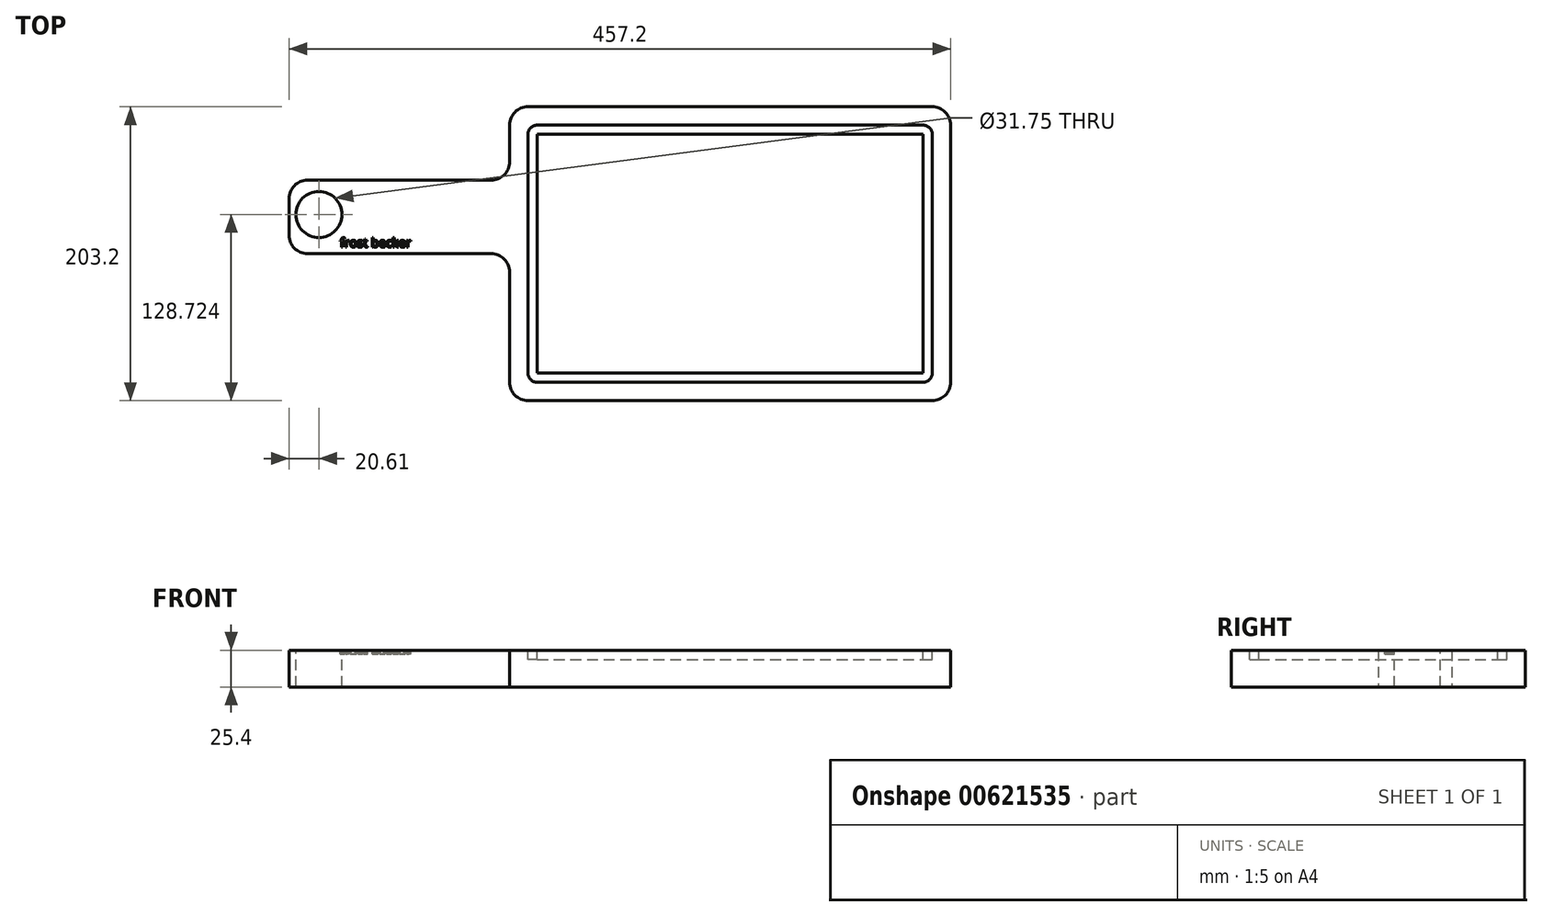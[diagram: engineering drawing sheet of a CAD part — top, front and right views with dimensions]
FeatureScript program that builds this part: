
annotation { "Feature Type Name" : "Feature", "Feature Type Description" : "" }
export const myFeature = defineFeature(function(context is Context, id is Id, definition is map)
    precondition{}
    {
        {
            var Q0;
            Q0=qCreatedBy(makeId("Top.planeOp"),FACE);
            var sketch = newSketch(context, id + "F0", { "sketchPlane" : qUnion([Q0])});
            skLineSegment(sketch, "E0.bottom", {"start": v(0, 0) * mm, "end": v(304.8, 0) * mm});
            skLineSegment(sketch, "E0.top", {"start": v(0, 203.2) * mm, "end": v(304.8, 203.2) * mm});
            skLineSegment(sketch, "E0.left", {"start": v(0, 0) * mm, "end": v(0, 203.2) * mm});
            skLineSegment(sketch, "E0.right", {"start": v(304.8, 0) * mm, "end": v(304.8, 203.2) * mm});
            skLineSegment(sketch, "E1.bottom", {"start": v(0, 101.6) * mm, "end": v(-152.4, 101.6) * mm});
            skLineSegment(sketch, "E1.top", {"start": v(0, 152.4) * mm, "end": v(-152.4, 152.4) * mm});
            skLineSegment(sketch, "E1.left", {"start": v(0, 101.6) * mm, "end": v(0, 152.4) * mm});
            skLineSegment(sketch, "E1.right", {"start": v(-152.4, 101.6) * mm, "end": v(-152.4, 152.4) * mm});
            skSolve(sketch);
        }
        {
            var Q0;
            Q0=makeQuery(id+"F0.imprint","IMPRINT",FACE,{"disambiguationData":[TD([[makeQuery(id+"F0.imprint","IMPRINT",EDGE,{"derivedFrom":sQuery(id+"F0.wireOp",EDGE,"E1.bottom")}),-1.0]])]});
            var Q1;
            {var subQ3=sQuery(id+"F0.wireOp",EDGE,"E0.bottom");Q1=makeQuery(id+"F0.imprint","IMPRINT",FACE,{"disambiguationData":[TD([[makeQuery(id+"F0.imprint","IMPRINT",EDGE,{"derivedFrom":subQ3}),1.0]])]});}
            extrude(context, id + "F1", {"entities" : qUnion([Q0, Q1]), "depth" : 25.4 * mm, "offsetDistance" : 25.4 * mm});
        }
        {
            var Q0;
            Q0=makeQuery(id+"F1.opExtrude","CAP_FACE",FACE,{"disambiguationData":[OSD([sQuery(id+"F0.wireOp",EDGE,"E0.bottom"),sQuery(id+"F0.wireOp",EDGE,"E0.top"),sQuery(id+"F0.wireOp",EDGE,"E0.left"),sQuery(id+"F0.wireOp",EDGE,"E0.right"),sQuery(id+"F0.wireOp",EDGE,"E1.bottom"),sQuery(id+"F0.wireOp",EDGE,"E1.top"),sQuery(id+"F0.wireOp",EDGE,"E1.right")])],"isStart":false});
            var sketch = newSketch(context, id + "F2", { "sketchPlane" : qUnion([Q0])});
            skCircle(sketch, "E2", {"center": v(-131.8, 128.72) * mm, "radius": 15.88 * mm});
            skLineSegment(sketch, "E3.0", {"start": v(12.7, 12.7) * mm, "end": v(12.7, 101.6) * mm});
            skLineSegment(sketch, "E3.1", {"start": v(12.7, 152.4) * mm, "end": v(12.7, 190.5) * mm});
            skLineSegment(sketch, "E3.2", {"start": v(12.7, 190.5) * mm, "end": v(292.1, 190.5) * mm});
            skLineSegment(sketch, "E3.3", {"start": v(292.1, 12.7) * mm, "end": v(292.1, 190.5) * mm});
            skLineSegment(sketch, "E3.4", {"start": v(12.7, 12.7) * mm, "end": v(292.1, 12.7) * mm});
            skLineSegment(sketch, "E4", {"start": v(12.7, 152.4) * mm, "end": v(12.7, 101.6) * mm});
            skLineSegment(sketch, "E5.0", {"start": v(19.05, 152.4) * mm, "end": v(19.05, 184.15) * mm});
            skLineSegment(sketch, "E5.1", {"start": v(285.75, 19.05) * mm, "end": v(285.75, 184.15) * mm});
            skLineSegment(sketch, "E5.2", {"start": v(19.05, 19.05) * mm, "end": v(285.75, 19.05) * mm});
            skLineSegment(sketch, "E5.3", {"start": v(19.05, 184.15) * mm, "end": v(285.75, 184.15) * mm});
            skLineSegment(sketch, "E5.4", {"start": v(19.05, 19.05) * mm, "end": v(19.05, 101.6) * mm});
            skLineSegment(sketch, "E5.5", {"start": v(19.05, 152.4) * mm, "end": v(19.05, 101.6) * mm});
            skSolve(sketch);
        }
        {
            var Q0;
            Q0=makeQuery(id+"F2.imprint","IMPRINT",FACE,{"disambiguationData":[TD([[makeQuery(id+"F2.imprint","IMPRINT",EDGE,{"derivedFrom":sQuery(id+"F2.wireOp",EDGE,"E2")}),1.0]])]});
            extrude(context, id + "F3", {"entities" : qUnion([Q0]), "operationType" : NewBodyOperationType.REMOVE, "oppositeDirection" : true, "depth" : 25.4 * mm, "offsetDistance" : 25.4 * mm});
        }
        {
            var Q0;
            Q0 = qSketchRegion(id + "F2", true);
            extrude(context, id + "F4", {"entities" : qUnion([Q0]), "operationType" : NewBodyOperationType.REMOVE, "oppositeDirection" : true, "depth" : 6.35 * mm, "offsetDistance" : 25.4 * mm});
        }
        {
            var Q0;
            Q0=makeQuery(id+"F4.boolean.opBoolean","COPY",EDGE,{"derivedFrom":makeQuery(id+"F4.opExtrude","SWEPT_EDGE",EDGE,{"disambiguationData":[OSD([sQuery(id+"F2.wireOp",EDGE,"E3.1"),sQuery(id+"F2.wireOp",EDGE,"E3.2")])]})});
            var Q1;
            Q1=makeQuery(id+"F4.boolean.opBoolean","COPY",EDGE,{"derivedFrom":makeQuery(id+"F4.opExtrude","SWEPT_EDGE",EDGE,{"disambiguationData":[OSD([sQuery(id+"F2.wireOp",EDGE,"E3.0"),sQuery(id+"F2.wireOp",EDGE,"E3.4")])]})});
            var Q2;
            Q2=makeQuery(id+"F4.boolean.opBoolean","COPY",EDGE,{"derivedFrom":makeQuery(id+"F4.opExtrude","SWEPT_EDGE",EDGE,{"disambiguationData":[OSD([sQuery(id+"F2.wireOp",EDGE,"E3.2"),sQuery(id+"F2.wireOp",EDGE,"E3.3")])]})});
            var Q3;
            Q3=makeQuery(id+"F4.boolean.opBoolean","COPY",EDGE,{"derivedFrom":makeQuery(id+"F4.opExtrude","SWEPT_EDGE",EDGE,{"disambiguationData":[OSD([sQuery(id+"F2.wireOp",EDGE,"E3.3"),sQuery(id+"F2.wireOp",EDGE,"E3.4")])]})});
            fillet(context, id + "F5", {"entities" : qUnion([Q0, Q1, Q2, Q3]), "radius" : 6.35 * mm, "tangentPropagation" : true, "allowEdgeOverflow" : false});
        }
        {
            var Q0;
            Q0=makeQuery(id+"F1.opExtrude","SWEPT_EDGE",EDGE,{"disambiguationData":[OSD([sQuery(id+"F0.wireOp",EDGE,"E0.top"),sQuery(id+"F0.wireOp",EDGE,"E0.left")])]});
            var Q1;
            Q1=makeQuery(id+"F1.opExtrude","SWEPT_EDGE",EDGE,{"disambiguationData":[OSD([sQuery(id+"F0.wireOp",EDGE,"E0.bottom"),sQuery(id+"F0.wireOp",EDGE,"E0.left")])]});
            var Q2;
            Q2=makeQuery(id+"F1.opExtrude","SWEPT_EDGE",EDGE,{"disambiguationData":[OSD([sQuery(id+"F0.wireOp",EDGE,"E1.top"),sQuery(id+"F0.wireOp",EDGE,"E1.right")])]});
            var Q3;
            Q3=makeQuery(id+"F1.opExtrude","SWEPT_EDGE",EDGE,{"disambiguationData":[OSD([sQuery(id+"F0.wireOp",EDGE,"E1.bottom"),sQuery(id+"F0.wireOp",EDGE,"E1.right")])]});
            var Q4;
            Q4=makeQuery(id+"F1.opExtrude","SWEPT_EDGE",EDGE,{"disambiguationData":[OSD([sQuery(id+"F0.wireOp",EDGE,"E0.bottom"),sQuery(id+"F0.wireOp",EDGE,"E0.right")])]});
            var Q5;
            Q5=makeQuery(id+"F1.opExtrude","SWEPT_EDGE",EDGE,{"disambiguationData":[OSD([sQuery(id+"F0.wireOp",EDGE,"E0.top"),sQuery(id+"F0.wireOp",EDGE,"E0.right")])]});
            var Q6;
            Q6=makeQuery(id+"F1.opExtrude","SWEPT_EDGE",EDGE,{"disambiguationData":[OSD([sQuery(id+"F0.wireOp",EDGE,"E0.left"),sQuery(id+"F0.wireOp",EDGE,"E1.top"),sQuery(id+"F0.wireOp",EDGE,"E1.left")])]});
            var Q7;
            Q7=makeQuery(id+"F1.opExtrude","SWEPT_EDGE",EDGE,{"disambiguationData":[OSD([sQuery(id+"F0.wireOp",EDGE,"E0.left"),sQuery(id+"F0.wireOp",EDGE,"E1.bottom"),sQuery(id+"F0.wireOp",EDGE,"E1.left")])]});
            fillet(context, id + "F6", {"entities" : qUnion([Q0, Q1, Q2, Q3, Q4, Q5, Q6, Q7]), "radius" : 12.7 * mm, "tangentPropagation" : true, "allowEdgeOverflow" : false});
        }
        {
            var Q0;
            {var subQ0=sQuery(id+"F0.wireOp",EDGE,"E1.right");var subQ1=sQuery(id+"F0.wireOp",EDGE,"E1.top");var subQ2=sQuery(id+"F0.wireOp",EDGE,"E1.bottom");var subQ3=sQuery(id+"F0.wireOp",EDGE,"E0.right");var subQ4=sQuery(id+"F0.wireOp",EDGE,"E0.bottom");var subQ5=sQuery(id+"F0.wireOp",EDGE,"E0.left");var subQ6=sQuery(id+"F0.wireOp",EDGE,"E0.top");Q0=makeQuery(id+"F4.boolean.opBoolean","SPLIT",FACE,{"disambiguationData":[TD([makeQuery(id+"F1.opExtrude","SWEPT_FACE",FACE,{"disambiguationData":[OSD([subQ4])]})])],"derivedFrom":makeQuery(id+"F1.opExtrude","CAP_FACE",FACE,{"disambiguationData":[OSD([subQ4,subQ6,subQ5,subQ3,subQ2,subQ1,subQ0])],"isStart":false})});}
            var sketch = newSketch(context, id + "F7", { "sketchPlane" : qUnion([Q0])});
            skText(sketch, "E6", { "text": "frost becker", "fontName": "OpenSans-Regular.ttf"});
            const initialGuessF7  = {"E6": [-0.11719, 0.10619, 1, 0, 0.00632]};
            skSetInitialGuess(sketch, initialGuessF7);
            skSolve(sketch);
        }
        {
            var Q0;
            Q0 = qSketchRegion(id + "F7", true);
            extrude(context, id + "F8", {"entities" : qUnion([Q0]), "operationType" : NewBodyOperationType.REMOVE, "oppositeDirection" : true, "depth" : 2.54 * mm, "offsetDistance" : 25.4 * mm});
        }
    });
